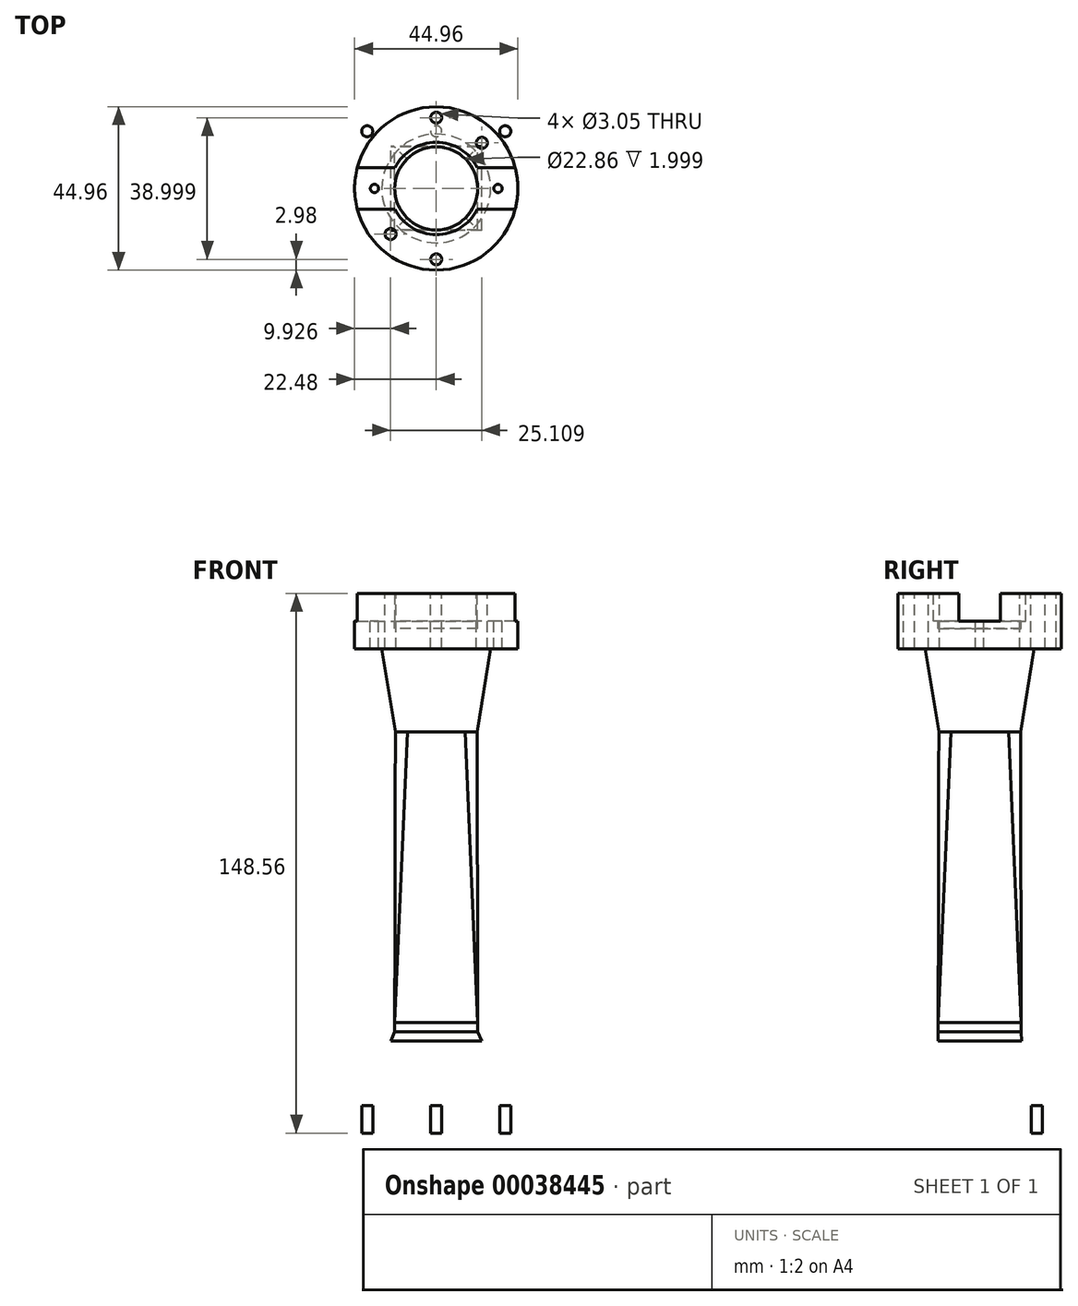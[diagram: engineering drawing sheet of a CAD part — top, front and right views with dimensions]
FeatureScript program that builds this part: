
annotation { "Feature Type Name" : "Feature", "Feature Type Description" : "" }
export const myFeature = defineFeature(function(context is Context, id is Id, definition is map)
    precondition{}
    {
        {
            var Q0;
            Q0=qCreatedBy(makeId("Top.planeOp"),FACE);
            var sketch = newSketch(context, id + "F0", { "sketchPlane" : qUnion([Q0])});
            skLineSegment(sketch, "E0.rect.bottom", {"start": v(24, 19) * mm, "end": v(-24, 19) * mm});
            skLineSegment(sketch, "E0.rect.top", {"start": v(24, -19) * mm, "end": v(-24, -19) * mm});
            skLineSegment(sketch, "E0.rect.left", {"start": v(24, 19) * mm, "end": v(24, -19) * mm});
            skLineSegment(sketch, "E0.rect.right", {"start": v(-24, 19) * mm, "end": v(-24, -19) * mm});
            skPoint(sketch, "E0.rect.middle", {"position": v(0, 0) * mm});
            skSolve(sketch);
        }
        {
            var Q0;
            Q0=qCreatedBy(makeId("Top.planeOp"),FACE);
            cPlane(context, id + "F1", {"entities" : qUnion([Q0]), "cplaneType" : CPlaneType.OFFSET, "offset" : 30.48 * mm, "width" : 152.4 * mm, "height" : 152.4 * mm});
        }
        {
            var Q0;
            Q0=qCreatedBy(id+"F1.planeOp",FACE);
            var sketch = newSketch(context, id + "F2", { "sketchPlane" : qUnion([Q0])});
            skCircle(sketch, "E1", {"center": v(0, 0) * mm, "radius": 11.25 * mm});
            skLineSegment(sketch, "E2.rect.bottom", {"start": v(11.43, -11.43) * mm, "end": v(-11.43, -11.43) * mm});
            skLineSegment(sketch, "E2.rect.top", {"start": v(11.43, 11.43) * mm, "end": v(-11.43, 11.43) * mm});
            skLineSegment(sketch, "E2.rect.left", {"start": v(11.43, -11.43) * mm, "end": v(11.43, 11.43) * mm});
            skLineSegment(sketch, "E2.rect.right", {"start": v(-11.43, -11.43) * mm, "end": v(-11.43, 11.43) * mm});
            skSolve(sketch);
        }
        {
            var Q0;
            Q0=qCreatedBy(id+"F1.planeOp",FACE);
            cPlane(context, id + "F3", {"entities" : qUnion([Q0]), "cplaneType" : CPlaneType.OFFSET, "offset" : 79.98 * mm, "width" : 152.4 * mm, "height" : 152.4 * mm});
        }
        {
            var Q0;
            Q0=qCreatedBy(id+"F3.planeOp",FACE);
            var sketch = newSketch(context, id + "F4", { "sketchPlane" : qUnion([Q0])});
            skCircle(sketch, "E3", {"center": v(0, 0) * mm, "radius": 11.25 * mm});
            skSolve(sketch);
        }
        {
            var Q0;
            Q0=qCreatedBy(makeId("Top.planeOp"),FACE);
            var Q1;
            Q1 = qBodyType(qCreatedBy(id + "F6" ,EDGE), BodyType.WIRE);
            cPlane(context, id + "F5", {"entities" : qUnion([Q0, Q1]), "cplaneType" : CPlaneType.OFFSET, "offset" : 7.62 * mm, "width" : 152.4 * mm, "height" : 152.4 * mm});
        }
        {
            var Q0;
            Q0=qCreatedBy(id+"F5.planeOp",FACE);
            var sketch = newSketch(context, id + "F6", { "sketchPlane" : qUnion([Q0])});
            skLineSegment(sketch, "E4.rect.bottom", {"start": v(-22.5, 18.5) * mm, "end": v(22.5, 18.5) * mm});
            skLineSegment(sketch, "E4.rect.top", {"start": v(-22.5, -18.5) * mm, "end": v(22.5, -18.5) * mm});
            skLineSegment(sketch, "E4.rect.left", {"start": v(-22.5, 18.5) * mm, "end": v(-22.5, -18.5) * mm});
            skLineSegment(sketch, "E4.rect.right", {"start": v(22.5, 18.5) * mm, "end": v(22.5, -18.5) * mm});
            skPoint(sketch, "E4.rect.middle", {"position": v(0, 0) * mm});
            skLineSegment(sketch, "E5.rect.bottom", {"start": v(20.32, -12.06) * mm, "end": v(-20.32, -12.06) * mm});
            skLineSegment(sketch, "E5.rect.top", {"start": v(20.32, 12.07) * mm, "end": v(-20.32, 12.07) * mm});
            skLineSegment(sketch, "E5.rect.left", {"start": v(20.32, -12.06) * mm, "end": v(20.32, 12.07) * mm});
            skLineSegment(sketch, "E5.rect.right", {"start": v(-20.32, -12.06) * mm, "end": v(-20.32, 12.07) * mm});
            skSolve(sketch);
        }
        {
            var Q0;
            Q0=qCreatedBy(id+"F3.planeOp",FACE);
            cPlane(context, id + "F7", {"entities" : qUnion([Q0]), "cplaneType" : CPlaneType.OFFSET, "offset" : 38.1 * mm, "width" : 152.4 * mm, "height" : 152.4 * mm});
        }
        {
            var Q0;
            Q0=qCreatedBy(id+"F7.planeOp",FACE);
            var sketch = newSketch(context, id + "F8", { "sketchPlane" : qUnion([Q0])});
            skCircle(sketch, "E6", {"center": v(0, 0) * mm, "radius": 22.48 * mm});
            skCircle(sketch, "E7", {"center": v(0, 0) * mm, "radius": 12.7 * mm});
            skLineSegment(sketch, "E8", {"start": v(11.32, 5.75) * mm, "end": v(21.73, 5.75) * mm});
            skLineSegment(sketch, "E9", {"start": v(11.32, -5.75) * mm, "end": v(21.73, -5.75) * mm});
            skLineSegment(sketch, "E10", {"start": v(-11.32, 5.75) * mm, "end": v(-21.73, 5.75) * mm});
            skLineSegment(sketch, "E11", {"start": v(-11.32, -5.75) * mm, "end": v(-21.73, -5.75) * mm});
            skSolve(sketch);
        }
        {
            var Q0;
            Q0=qCreatedBy(id+"F7.planeOp",FACE);
            cPlane(context, id + "F9", {"entities" : qUnion([Q0]), "cplaneType" : CPlaneType.OFFSET, "offset" : 7.62 * mm, "oppositeDirection" : true, "width" : 152.4 * mm, "height" : 152.4 * mm});
        }
        {
            var Q0;
            Q0=qCreatedBy(id+"F9.planeOp",FACE);
            var sketch = newSketch(context, id + "F10", { "sketchPlane" : qUnion([Q0])});
            skCircle(sketch, "E12", {"center": v(0, 0) * mm, "radius": 22.48 * mm});
            skCircle(sketch, "E13", {"center": v(0, 0) * mm, "radius": 14.99 * mm});
            skSolve(sketch);
        }
        {
            var Q0;
            Q0=makeQuery(id+"F2.imprint","IMPRINT",FACE,{"disambiguationData":[TD([[makeQuery(id+"F2.imprint","IMPRINT",EDGE,{"derivedFrom":sQuery(id+"F2.wireOp",EDGE,"E1")}),-1.0]])]});
            var Q1;
            Q1=makeQuery(id+"F2.imprint","IMPRINT",FACE,{"disambiguationData":[TD([[makeQuery(id+"F2.imprint","IMPRINT",EDGE,{"derivedFrom":sQuery(id+"F2.wireOp",EDGE,"E1")}),1.0]])]});
            extrude(context, id + "F11", {"entities" : qUnion([Q0, Q1]), "oppositeDirection" : true, "depth" : 2.54 * mm});
        }
        {
            var Q1;
            Q1=makeQuery(id+"F6.imprint","IMPRINT",FACE,{"disambiguationData":[TD([[makeQuery(id+"F6.imprint","IMPRINT",EDGE,{"derivedFrom":sQuery(id+"F6.wireOp",EDGE,"E5.rect.bottom")}),-1.0]])]});
            var Q2;
            Q2=makeQuery(id+"F11.opExtrude","CAP_FACE",FACE,{"disambiguationData":[OSD([sQuery(id+"F2.wireOp",EDGE,"E2.rect.bottom"),sQuery(id+"F2.wireOp",EDGE,"E2.rect.top"),sQuery(id+"F2.wireOp",EDGE,"E2.rect.left"),sQuery(id+"F2.wireOp",EDGE,"E2.rect.right")])],"isStart":false});
            loft(context, id + "F12", {"operationType" : NewBodyOperationType.ADD, "sheetProfilesArray" : [{ "sheetProfileEntities" : qUnion([Q1]) }, { "sheetProfileEntities" : qUnion([Q2]) }]});
        }
        {
            var Q1;
            Q1=makeQuery(id+"F4.imprint","IMPRINT",FACE,{"disambiguationData":[TD([[makeQuery(id+"F4.imprint","IMPRINT",EDGE,{"derivedFrom":sQuery(id+"F4.wireOp",EDGE,"E3")}),1.0]])]});
            var Q2;
            Q2=makeQuery(id+"F11.opExtrude","CAP_FACE",FACE,{"disambiguationData":[OSD([sQuery(id+"F2.wireOp",EDGE,"E2.rect.bottom"),sQuery(id+"F2.wireOp",EDGE,"E2.rect.top"),sQuery(id+"F2.wireOp",EDGE,"E2.rect.left"),sQuery(id+"F2.wireOp",EDGE,"E2.rect.right")])],"isStart":true});
            loft(context, id + "F13", {"operationType" : NewBodyOperationType.ADD, "sheetProfilesArray" : [{ "sheetProfileEntities" : qUnion([Q1]) }, { "sheetProfileEntities" : qUnion([Q2]) }]});
        }
        {
            var Q0;
            Q0=makeQuery(id+"F0.imprint","IMPRINT",FACE,{"disambiguationData":[TD([[makeQuery(id+"F0.imprint","IMPRINT",EDGE,{"derivedFrom":sQuery(id+"F0.wireOp",EDGE,"E0.rect.bottom")}),1.0]])]});
            var Q1;
            Q1=makeQuery(id+"F12.opLoft","CAP_FACE",FACE,{"disambiguationData":[OSD([makeQuery(id+"F6.imprint","IMPRINT",FACE,{"disambiguationData":[TD([[makeQuery(id+"F6.imprint","IMPRINT",EDGE,{"derivedFrom":sQuery(id+"F6.wireOp",EDGE,"E5.rect.bottom")}),-1.0]])]})])],"isStart":true});
            extrude(context, id + "F14", {"entities" : qUnion([Q0]), "operationType" : NewBodyOperationType.ADD, "endBound" : BoundingType.UP_TO_SURFACE, "endBoundEntityFace" : qUnion([Q1]), "depth" : 25.4 * mm});
        }
        {
            var Q0;
            Q0=qCreatedBy(id+"F9.planeOp",FACE);
            cPlane(context, id + "F15", {"entities" : qUnion([Q0]), "cplaneType" : CPlaneType.OFFSET, "offset" : 7.62 * mm, "oppositeDirection" : true, "width" : 152.4 * mm, "height" : 152.4 * mm});
        }
        {
            var Q0;
            Q0=qCreatedBy(id+"F15.planeOp",FACE);
            var sketch = newSketch(context, id + "F16", { "sketchPlane" : qUnion([Q0])});
            skCircle(sketch, "E14", {"center": v(0, 0) * mm, "radius": 14.99 * mm});
            skSolve(sketch);
        }
        {
            var Q1;
            Q1=makeQuery(id+"F13.opLoft","CAP_FACE",FACE,{"disambiguationData":[OSD([makeQuery(id+"F4.imprint","IMPRINT",FACE,{"disambiguationData":[TD([[makeQuery(id+"F4.imprint","IMPRINT",EDGE,{"derivedFrom":sQuery(id+"F4.wireOp",EDGE,"E3")}),1.0]])]})])],"isStart":true});
            var Q2;
            Q2=makeQuery(id+"F16.imprint","IMPRINT",FACE,{"disambiguationData":[TD([[makeQuery(id+"F16.imprint","IMPRINT",EDGE,{"derivedFrom":sQuery(id+"F16.wireOp",EDGE,"E14")}),1.0]])]});
            loft(context, id + "F17", {"operationType" : NewBodyOperationType.ADD, "sheetProfilesArray" : [{ "sheetProfileEntities" : qUnion([Q1]) }, { "sheetProfileEntities" : qUnion([Q2]) }]});
        }
        {
            var Q0;
            Q0=makeQuery(id+"F10.imprint","IMPRINT",FACE,{"disambiguationData":[TD([[makeQuery(id+"F10.imprint","IMPRINT",EDGE,{"derivedFrom":sQuery(id+"F10.wireOp",EDGE,"E12")}),1.0]])]});
            var Q1;
            Q1=makeQuery(id+"F10.imprint","IMPRINT",FACE,{"disambiguationData":[TD([[makeQuery(id+"F10.imprint","IMPRINT",EDGE,{"derivedFrom":sQuery(id+"F10.wireOp",EDGE,"E13")}),1.0]])]});
            var Q2;
            Q2=makeQuery(id+"F17.opLoft","CAP_FACE",FACE,{"disambiguationData":[OSD([makeQuery(id+"F16.imprint","IMPRINT",FACE,{"disambiguationData":[TD([[makeQuery(id+"F16.imprint","IMPRINT",EDGE,{"derivedFrom":sQuery(id+"F16.wireOp",EDGE,"E14")}),1.0]])]})])],"isStart":true});
            extrude(context, id + "F18", {"entities" : qUnion([Q0, Q1]), "operationType" : NewBodyOperationType.ADD, "endBound" : BoundingType.UP_TO_SURFACE, "oppositeDirection" : true, "endBoundEntityFace" : qUnion([Q2]), "depth" : 25.4 * mm});
        }
        {
            var Q0;
            {var subQ1=sQuery(id+"F8.wireOp",EDGE,"E9");Q0=makeQuery(id+"F8.imprint","IMPRINT",FACE,{"disambiguationData":[TD([[makeQuery(id+"F8.imprint","IMPRINT",EDGE,{"derivedFrom":subQ1}),-1.0]])]});}
            var Q1;
            {var subQ1=sQuery(id+"F8.wireOp",EDGE,"E8");Q1=makeQuery(id+"F8.imprint","IMPRINT",FACE,{"disambiguationData":[TD([[makeQuery(id+"F8.imprint","IMPRINT",EDGE,{"derivedFrom":subQ1}),1.0]])]});}
            var Q2;
            Q2=makeQuery(id+"F18.opExtrude","CAP_FACE",FACE,{"disambiguationData":[OSD([sQuery(id+"F10.wireOp",EDGE,"E12")])],"isStart":true});
            extrude(context, id + "F19", {"entities" : qUnion([Q0, Q1]), "operationType" : NewBodyOperationType.ADD, "endBound" : BoundingType.UP_TO_SURFACE, "oppositeDirection" : true, "endBoundEntityFace" : qUnion([Q2]), "depth" : 25.4 * mm});
        }
        {
            var Q0;
            Q0=makeQuery(id+"F18.opExtrude","CAP_FACE",FACE,{"disambiguationData":[OSD([sQuery(id+"F10.wireOp",EDGE,"E12")])],"isStart":true});
            var sketch = newSketch(context, id + "F20", { "sketchPlane" : qUnion([Q0])});
            skPoint(sketch, "E15", {"position": v(17, 0) * mm});
            skPoint(sketch, "E16", {"position": v(-17, 0) * mm});
            skCircle(sketch, "E17", {"center": v(17, 0) * mm, "radius": 1.14 * mm});
            skCircle(sketch, "E18", {"center": v(-17, 0) * mm, "radius": 1.14 * mm});
            skSolve(sketch);
        }
        {
            var Q0;
            Q0=makeQuery(id+"F14.opExtrude","CAP_FACE",FACE,{"disambiguationData":[OSD([sQuery(id+"F0.wireOp",EDGE,"E0.rect.bottom"),sQuery(id+"F0.wireOp",EDGE,"E0.rect.top"),sQuery(id+"F0.wireOp",EDGE,"E0.rect.left"),sQuery(id+"F0.wireOp",EDGE,"E0.rect.right")])],"isStart":true});
            var sketch = newSketch(context, id + "F21", { "sketchPlane" : qUnion([Q0])});
            skPoint(sketch, "E19", {"position": v(0, 15.75) * mm});
            skPoint(sketch, "E19.positionSnap0", {"position": v(0, 19) * mm});
            skPoint(sketch, "E20", {"position": v(0, -15.75) * mm});
            skPoint(sketch, "E21", {"position": v(19, -15.75) * mm});
            skPoint(sketch, "E22", {"position": v(-19, -15.75) * mm});
            skPoint(sketch, "E23.MirrorP", {"position": v(-19, 15.75) * mm});
            skPoint(sketch, "E24.MirrorP", {"position": v(19, 15.75) * mm});
            skCircle(sketch, "E25", {"center": v(-19, 15.75) * mm, "radius": 1.52 * mm});
            skCircle(sketch, "E26", {"center": v(0, 15.75) * mm, "radius": 1.52 * mm});
            skCircle(sketch, "E27", {"center": v(19, 15.75) * mm, "radius": 1.52 * mm});
            skCircle(sketch, "E28.MirrorC", {"center": v(-19, -15.75) * mm, "radius": 1.52 * mm});
            skCircle(sketch, "E29.MirrorC", {"center": v(0, -15.75) * mm, "radius": 1.52 * mm});
            skCircle(sketch, "E30.MirrorC", {"center": v(19, -15.75) * mm, "radius": 1.52 * mm});
            skSolve(sketch);
        }
        {
            var Q0;
            Q0=makeQuery(id+"F21.imprint","IMPRINT",FACE,{"disambiguationData":[TD([[makeQuery(id+"F21.imprint","IMPRINT",EDGE,{"derivedFrom":sQuery(id+"F21.wireOp",EDGE,"E25")}),1.0]])]});
            var Q1;
            Q1=makeQuery(id+"F21.imprint","IMPRINT",FACE,{"disambiguationData":[TD([[makeQuery(id+"F21.imprint","IMPRINT",EDGE,{"derivedFrom":sQuery(id+"F21.wireOp",EDGE,"E26")}),1.0]])]});
            var Q2;
            Q2=makeQuery(id+"F21.imprint","IMPRINT",FACE,{"disambiguationData":[TD([[makeQuery(id+"F21.imprint","IMPRINT",EDGE,{"derivedFrom":sQuery(id+"F21.wireOp",EDGE,"E27")}),1.0]])]});
            var Q3;
            Q3=makeQuery(id+"F21.imprint","IMPRINT",FACE,{"disambiguationData":[TD([[makeQuery(id+"F21.imprint","IMPRINT",EDGE,{"derivedFrom":sQuery(id+"F21.wireOp",EDGE,"E28.MirrorC")}),-1.0]])]});
            var Q4;
            Q4=makeQuery(id+"F21.imprint","IMPRINT",FACE,{"disambiguationData":[TD([[makeQuery(id+"F21.imprint","IMPRINT",EDGE,{"derivedFrom":sQuery(id+"F21.wireOp",EDGE,"E29.MirrorC")}),-1.0]])]});
            var Q5;
            Q5=makeQuery(id+"F21.imprint","IMPRINT",FACE,{"disambiguationData":[TD([[makeQuery(id+"F21.imprint","IMPRINT",EDGE,{"derivedFrom":sQuery(id+"F21.wireOp",EDGE,"E30.MirrorC")}),-1.0]])]});
            extrude(context, id + "F22", {"entities" : qUnion([Q0, Q1, Q2, Q3, Q4, Q5]), "operationType" : NewBodyOperationType.REMOVE, "oppositeDirection" : true, "depth" : 25.4 * mm});
        }
        {
            var Q0;
            Q0=makeQuery(id+"F19.opExtrude","CAP_FACE",FACE,{"disambiguationData":[OSD([sQuery(id+"F8.wireOp",EDGE,"E6"),sQuery(id+"F8.wireOp",EDGE,"E7"),sQuery(id+"F8.wireOp",EDGE,"E8"),sQuery(id+"F8.wireOp",EDGE,"E10")])],"isStart":true});
            var sketch = newSketch(context, id + "F23", { "sketchPlane" : qUnion([Q0])});
            skPoint(sketch, "E31", {"position": v(0, -19.5) * mm});
            skPoint(sketch, "E32", {"position": v(0, 19.5) * mm});
            skLineSegment(sketch, "E33", {"start": v(0, 19.5) * mm, "end": v(0, -19.5) * mm, "construction": true});
            skLineSegment(sketch, "E34", {"start": v(28.92, 28.92) * mm, "end": v(-22.07, -22.07) * mm, "construction": true});
            skPoint(sketch, "E35", {"position": v(-12.55, -12.55) * mm});
            skPoint(sketch, "E36", {"position": v(12.55, 12.55) * mm});
            skCircle(sketch, "E37", {"center": v(0, 19.5) * mm, "radius": 1.52 * mm});
            skCircle(sketch, "E38", {"center": v(12.55, 12.55) * mm, "radius": 1.52 * mm});
            skCircle(sketch, "E39", {"center": v(0, -19.5) * mm, "radius": 1.52 * mm});
            skCircle(sketch, "E40", {"center": v(-12.55, -12.55) * mm, "radius": 1.52 * mm});
            skSolve(sketch);
        }
        {
            var Q0;
            Q0=makeQuery(id+"F23.imprint","IMPRINT",FACE,{"disambiguationData":[TD([[makeQuery(id+"F23.imprint","IMPRINT",EDGE,{"derivedFrom":sQuery(id+"F23.wireOp",EDGE,"E37")}),1.0]])]});
            var Q1;
            Q1=makeQuery(id+"F23.imprint","IMPRINT",FACE,{"disambiguationData":[TD([[makeQuery(id+"F23.imprint","IMPRINT",EDGE,{"derivedFrom":sQuery(id+"F23.wireOp",EDGE,"E38")}),1.0]])]});
            var Q2;
            Q2=makeQuery(id+"F23.imprint","IMPRINT",FACE,{"disambiguationData":[TD([[makeQuery(id+"F23.imprint","IMPRINT",EDGE,{"derivedFrom":sQuery(id+"F23.wireOp",EDGE,"E39")}),1.0]])]});
            var Q3;
            Q3=makeQuery(id+"F23.imprint","IMPRINT",FACE,{"disambiguationData":[TD([[makeQuery(id+"F23.imprint","IMPRINT",EDGE,{"derivedFrom":sQuery(id+"F23.wireOp",EDGE,"E40")}),1.0]])]});
            extrude(context, id + "F24", {"entities" : qUnion([Q0, Q1, Q2, Q3]), "operationType" : NewBodyOperationType.REMOVE, "oppositeDirection" : true, "depth" : 25.4 * mm});
        }
        {
            var Q0;
            Q0=makeQuery(id+"F20.imprint","IMPRINT",FACE,{"disambiguationData":[TD([[makeQuery(id+"F20.imprint","IMPRINT",EDGE,{"derivedFrom":sQuery(id+"F20.wireOp",EDGE,"E17")}),1.0]])]});
            var Q1;
            Q1=makeQuery(id+"F20.imprint","IMPRINT",FACE,{"disambiguationData":[TD([[makeQuery(id+"F20.imprint","IMPRINT",EDGE,{"derivedFrom":sQuery(id+"F20.wireOp",EDGE,"E18")}),1.0]])]});
            extrude(context, id + "F25", {"entities" : qUnion([Q0, Q1]), "operationType" : NewBodyOperationType.REMOVE, "oppositeDirection" : true, "depth" : 25.4 * mm});
        }
        {
            var Q0;
            Q0=makeQuery(id+"F18.opExtrude","CAP_FACE",FACE,{"disambiguationData":[OSD([sQuery(id+"F10.wireOp",EDGE,"E12")])],"isStart":true});
            var sketch = newSketch(context, id + "F26", { "sketchPlane" : qUnion([Q0])});
            skCircle(sketch, "E41", {"center": v(0, 0) * mm, "radius": 11.43 * mm});
            skSolve(sketch);
        }
        {
            var Q0;
            Q0=makeQuery(id+"F26.imprint","IMPRINT",FACE,{"disambiguationData":[TD([[makeQuery(id+"F26.imprint","IMPRINT",EDGE,{"derivedFrom":sQuery(id+"F26.wireOp",EDGE,"E41")}),1.0]])]});
            extrude(context, id + "F27", {"entities" : qUnion([Q0]), "operationType" : NewBodyOperationType.REMOVE, "oppositeDirection" : true, "depth" : 2 * mm});
        }
    });
